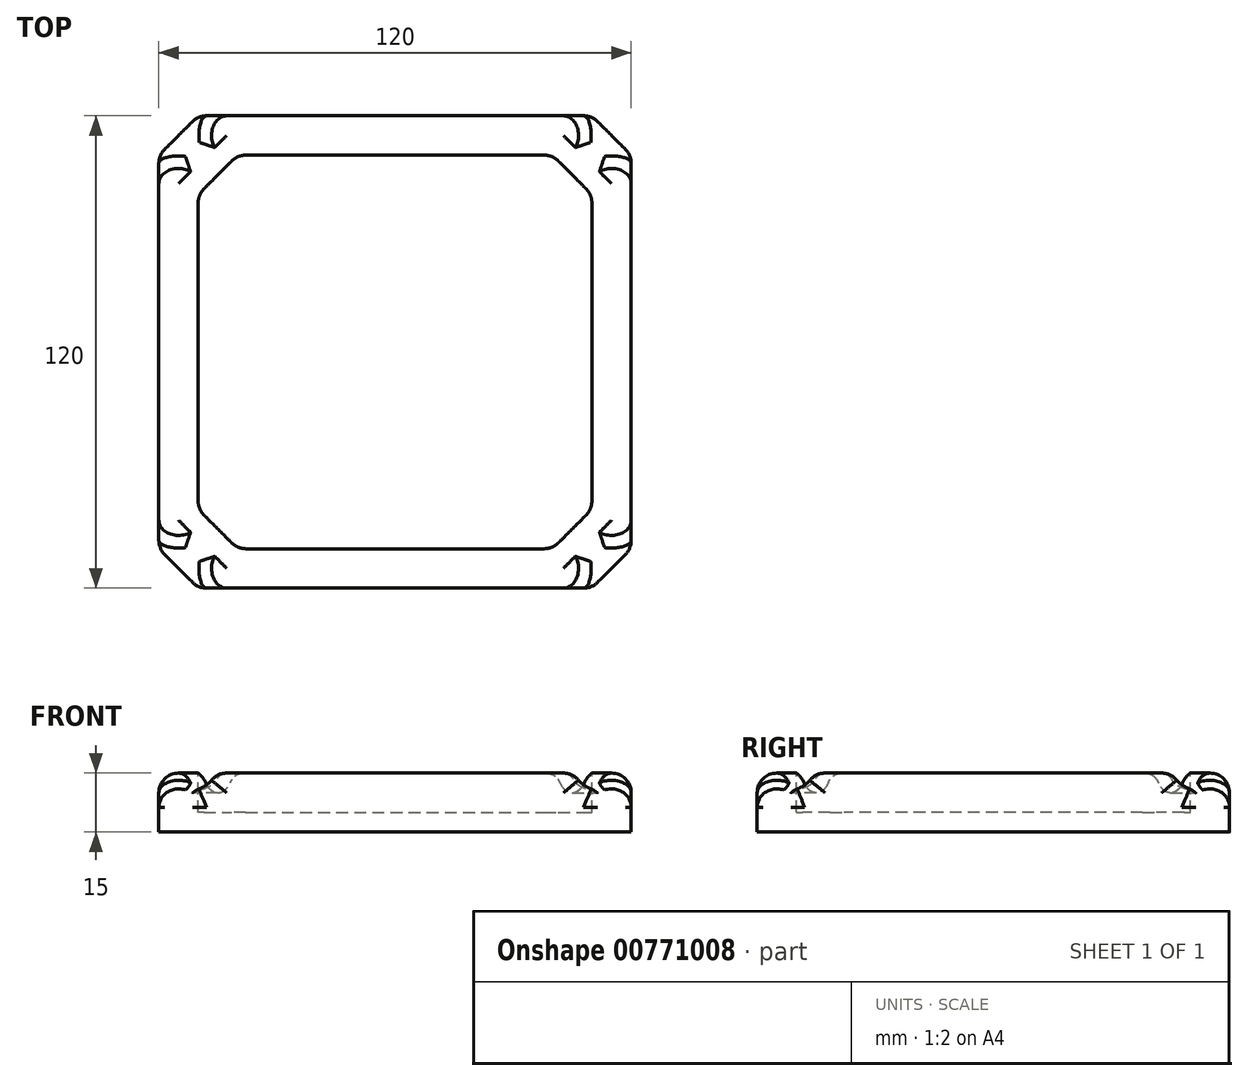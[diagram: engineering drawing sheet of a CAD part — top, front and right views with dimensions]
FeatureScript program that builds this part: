
annotation { "Feature Type Name" : "Feature", "Feature Type Description" : "" }
export const myFeature = defineFeature(function(context is Context, id is Id, definition is map)
    precondition{}
    {
        {
            var Q0;
            Q0=qCreatedBy(makeId("Top.planeOp"),FACE);
            var sketch = newSketch(context, id + "F0", { "sketchPlane" : qUnion([Q0])});
            skLineSegment(sketch, "E0.bottom", {"start": v(-50, 60) * mm, "end": v(50, 60) * mm});
            skLineSegment(sketch, "E0.top", {"start": v(-50, -60) * mm, "end": v(50, -60) * mm});
            skLineSegment(sketch, "E0.left", {"start": v(-60, 50) * mm, "end": v(-60, -50) * mm});
            skLineSegment(sketch, "E0.right", {"start": v(60, 50) * mm, "end": v(60, -50) * mm});
            skLineSegment(sketch, "E1", {"start": v(-60, 50) * mm, "end": v(-50, 60) * mm});
            skLineSegment(sketch, "E2", {"start": v(50, 60) * mm, "end": v(60, 50) * mm});
            skLineSegment(sketch, "E3", {"start": v(60, -50) * mm, "end": v(50, -60) * mm});
            skLineSegment(sketch, "E4", {"start": v(-60, -50) * mm, "end": v(-50, -60) * mm});
            skSolve(sketch);
        }
        {
            var Q0;
            Q0=makeQuery(id+"F0.imprint","IMPRINT",FACE,{"disambiguationData":[TD([[makeQuery(id+"F0.imprint","IMPRINT",EDGE,{"derivedFrom":sQuery(id+"F0.wireOp",EDGE,"E0.bottom")}),-1.0]])]});
            extrude(context, id + "F1", {"entities" : qUnion([Q0]), "depth" : 15 * mm, "offsetDistance" : 25 * mm});
        }
        {
            var Q0;
            Q0=makeQuery(id+"F1.opExtrude","CAP_FACE",FACE,{"disambiguationData":[OSD([sQuery(id+"F0.wireOp",EDGE,"E0.bottom"),sQuery(id+"F0.wireOp",EDGE,"E0.top"),sQuery(id+"F0.wireOp",EDGE,"E0.left"),sQuery(id+"F0.wireOp",EDGE,"E0.right"),sQuery(id+"F0.wireOp",EDGE,"E1"),sQuery(id+"F0.wireOp",EDGE,"E2"),sQuery(id+"F0.wireOp",EDGE,"E3"),sQuery(id+"F0.wireOp",EDGE,"E4")])],"isStart":false});
            var sketch = newSketch(context, id + "F2", { "sketchPlane" : qUnion([Q0])});
            skLineSegment(sketch, "E5.bottom", {"start": v(-40, 50) * mm, "end": v(40, 50) * mm});
            skLineSegment(sketch, "E5.top", {"start": v(-40, -50) * mm, "end": v(40, -50) * mm});
            skLineSegment(sketch, "E5.left", {"start": v(-50, 40) * mm, "end": v(-50, -40) * mm});
            skLineSegment(sketch, "E5.right", {"start": v(50, 40) * mm, "end": v(50, -40) * mm});
            skLineSegment(sketch, "E6", {"start": v(-50, 40) * mm, "end": v(-40, 50) * mm});
            skLineSegment(sketch, "E7", {"start": v(40, 50) * mm, "end": v(50, 40) * mm});
            skLineSegment(sketch, "E8", {"start": v(50, -40) * mm, "end": v(40, -50) * mm});
            skLineSegment(sketch, "E9", {"start": v(-50, -40) * mm, "end": v(-40, -50) * mm});
            skSolve(sketch);
        }
        {
            var Q0;
            Q0=makeQuery(id+"F2.imprint","IMPRINT",FACE,{"disambiguationData":[TD([[makeQuery(id+"F2.imprint","IMPRINT",EDGE,{"derivedFrom":sQuery(id+"F2.wireOp",EDGE,"E5.bottom")}),-1.0]])]});
            extrude(context, id + "F3", {"entities" : qUnion([Q0]), "operationType" : NewBodyOperationType.REMOVE, "oppositeDirection" : true, "depth" : 10 * mm, "offsetDistance" : 25 * mm});
        }
        {
            var Q0;
            Q0=makeQuery(id+"F1.opExtrude","SWEPT_FACE",FACE,{"disambiguationData":[OSD([sQuery(id+"F0.wireOp",EDGE,"E1")])]});
            cPlane(context, id + "F4", {"entities" : qUnion([Q0]), "cplaneType" : CPlaneType.OFFSET, "offset" : .1 * mm, "width" : 150 * mm, "height" : 150 * mm});
        }
        {
            var Q0;
            Q0=qCreatedBy(id+"F4.planeOp",FACE);
            var sketch = newSketch(context, id + "F5", { "sketchPlane" : qUnion([Q0])});
            skCircle(sketch, "E10", {"center": v(0, 15) * mm, "radius": 5 * mm});
            skSolve(sketch);
        }
        {
            var Q0;
            Q0=makeQuery(id+"F5.imprint","IMPRINT",FACE,{"disambiguationData":[TD([[makeQuery(id+"F5.imprint","IMPRINT",EDGE,{"derivedFrom":sQuery(id+"F5.wireOp",EDGE,"E10")}),1.0]])]});
            extrude(context, id + "F6", {"entities" : qUnion([Q0]), "operationType" : NewBodyOperationType.REMOVE, "oppositeDirection" : true, "depth" : 15 * mm, "offsetDistance" : 25 * mm});
        }
        {
            var Q0;
            Q0=makeQuery(id+"F1.opExtrude","SWEPT_FACE",FACE,{"disambiguationData":[OSD([sQuery(id+"F0.wireOp",EDGE,"E2")])]});
            cPlane(context, id + "F7", {"entities" : qUnion([Q0]), "cplaneType" : CPlaneType.OFFSET, "offset" : .1 * mm, "width" : 150 * mm, "height" : 150 * mm});
        }
        {
            var Q0;
            Q0=qCreatedBy(id+"F7.planeOp",FACE);
            var sketch = newSketch(context, id + "F8", { "sketchPlane" : qUnion([Q0])});
            skCircle(sketch, "E11", {"center": v(0, 15) * mm, "radius": 5 * mm});
            skSolve(sketch);
        }
        {
            var Q0;
            Q0=makeQuery(id+"F8.imprint","IMPRINT",FACE,{"disambiguationData":[TD([[makeQuery(id+"F8.imprint","IMPRINT",EDGE,{"derivedFrom":sQuery(id+"F8.wireOp",EDGE,"E11")}),1.0]])]});
            extrude(context, id + "F9", {"entities" : qUnion([Q0]), "operationType" : NewBodyOperationType.REMOVE, "oppositeDirection" : true, "depth" : 15 * mm, "offsetDistance" : 25 * mm});
        }
        {
            var Q0;
            Q0=makeQuery(id+"F1.opExtrude","SWEPT_FACE",FACE,{"disambiguationData":[OSD([sQuery(id+"F0.wireOp",EDGE,"E3")])]});
            cPlane(context, id + "F10", {"entities" : qUnion([Q0]), "cplaneType" : CPlaneType.OFFSET, "offset" : .1 * mm, "width" : 150 * mm, "height" : 150 * mm});
        }
        {
            var Q0;
            Q0=qCreatedBy(id+"F10.planeOp",FACE);
            var sketch = newSketch(context, id + "F11", { "sketchPlane" : qUnion([Q0])});
            skCircle(sketch, "E12", {"center": v(0, 15) * mm, "radius": 5 * mm});
            skSolve(sketch);
        }
        {
            var Q0;
            Q0=makeQuery(id+"F11.imprint","IMPRINT",FACE,{"disambiguationData":[TD([[makeQuery(id+"F11.imprint","IMPRINT",EDGE,{"derivedFrom":sQuery(id+"F11.wireOp",EDGE,"E12")}),1.0]])]});
            extrude(context, id + "F12", {"entities" : qUnion([Q0]), "operationType" : NewBodyOperationType.REMOVE, "oppositeDirection" : true, "depth" : 15 * mm, "offsetDistance" : 25 * mm});
        }
        {
            var Q0;
            Q0=makeQuery(id+"F1.opExtrude","SWEPT_FACE",FACE,{"disambiguationData":[OSD([sQuery(id+"F0.wireOp",EDGE,"E4")])]});
            cPlane(context, id + "F13", {"entities" : qUnion([Q0]), "cplaneType" : CPlaneType.OFFSET, "offset" : .1 * mm, "width" : 150 * mm, "height" : 150 * mm});
        }
        {
            var Q0;
            Q0=qCreatedBy(id+"F13.planeOp",FACE);
            var sketch = newSketch(context, id + "F14", { "sketchPlane" : qUnion([Q0])});
            skCircle(sketch, "E13", {"center": v(0, 15) * mm, "radius": 5 * mm});
            skSolve(sketch);
        }
        {
            var Q0;
            Q0=makeQuery(id+"F14.imprint","IMPRINT",FACE,{"disambiguationData":[TD([[makeQuery(id+"F14.imprint","IMPRINT",EDGE,{"derivedFrom":sQuery(id+"F14.wireOp",EDGE,"E13")}),1.0]])]});
            extrude(context, id + "F15", {"entities" : qUnion([Q0]), "operationType" : NewBodyOperationType.REMOVE, "oppositeDirection" : true, "depth" : 15 * mm, "offsetDistance" : 25 * mm});
        }
        {
            var Q0;
            Q0=makeQuery(id+"F6.boolean.opBoolean","INTERSECT",EDGE,{"disambiguationData":[OD(1.0)],"derivedFrom":[makeQuery(id+"F1.opExtrude","CAP_FACE",FACE,{"disambiguationData":[OSD([sQuery(id+"F0.wireOp",EDGE,"E0.bottom"),sQuery(id+"F0.wireOp",EDGE,"E0.top"),sQuery(id+"F0.wireOp",EDGE,"E0.left"),sQuery(id+"F0.wireOp",EDGE,"E0.right"),sQuery(id+"F0.wireOp",EDGE,"E1"),sQuery(id+"F0.wireOp",EDGE,"E2"),sQuery(id+"F0.wireOp",EDGE,"E3"),sQuery(id+"F0.wireOp",EDGE,"E4")])],"isStart":false}),makeQuery(id+"F6.opExtrude","SWEPT_FACE",FACE,{"disambiguationData":[OSD([sQuery(id+"F5.wireOp",EDGE,"E10")])]})]});
            var Q1;
            Q1=makeQuery(id+"F6.boolean.opBoolean","INTERSECT",EDGE,{"disambiguationData":[OD(0.0)],"derivedFrom":[makeQuery(id+"F1.opExtrude","CAP_FACE",FACE,{"disambiguationData":[OSD([sQuery(id+"F0.wireOp",EDGE,"E0.bottom"),sQuery(id+"F0.wireOp",EDGE,"E0.top"),sQuery(id+"F0.wireOp",EDGE,"E0.left"),sQuery(id+"F0.wireOp",EDGE,"E0.right"),sQuery(id+"F0.wireOp",EDGE,"E1"),sQuery(id+"F0.wireOp",EDGE,"E2"),sQuery(id+"F0.wireOp",EDGE,"E3"),sQuery(id+"F0.wireOp",EDGE,"E4")])],"isStart":false}),makeQuery(id+"F6.opExtrude","SWEPT_FACE",FACE,{"disambiguationData":[OSD([sQuery(id+"F5.wireOp",EDGE,"E10")])]})]});
            var Q2;
            {var subQ5=sQuery(id+"F0.wireOp",EDGE,"E4");var subQ7=sQuery(id+"F0.wireOp",EDGE,"E0.top");var subQ8=makeQuery(id+"F1.opExtrude","SWEPT_FACE",FACE,{"disambiguationData":[OSD([subQ7])]});var subQ10=sQuery(id+"F0.wireOp",EDGE,"E3");var subQ12=sQuery(id+"F0.wireOp",EDGE,"E0.left");var subQ14=sQuery(id+"F0.wireOp",EDGE,"E1");var subQ16=sQuery(id+"F0.wireOp",EDGE,"E2");var subQ17=sQuery(id+"F0.wireOp",EDGE,"E0.right");Q2=makeQuery(id+"F15.boolean.opBoolean","INTERSECT",EDGE,{"disambiguationData":[OD(1.0)],"derivedFrom":[makeQuery(id+"F12.boolean.opBoolean","SPLIT",FACE,{"disambiguationData":[TD([subQ8])],"derivedFrom":makeQuery(id+"F9.boolean.opBoolean","SPLIT",FACE,{"disambiguationData":[TD([subQ8])],"derivedFrom":makeQuery(id+"F1.opExtrude","CAP_FACE",FACE,{"disambiguationData":[OSD([sQuery(id+"F0.wireOp",EDGE,"E0.bottom"),subQ7,subQ12,subQ17,subQ14,subQ16,subQ10,subQ5])],"isStart":false})})}),makeQuery(id+"F15.opExtrude","SWEPT_FACE",FACE,{"disambiguationData":[OSD([sQuery(id+"F14.wireOp",EDGE,"E13")])]})]});}
            var Q3;
            {var subQ5=sQuery(id+"F0.wireOp",EDGE,"E4");var subQ7=sQuery(id+"F0.wireOp",EDGE,"E0.top");var subQ8=makeQuery(id+"F1.opExtrude","SWEPT_FACE",FACE,{"disambiguationData":[OSD([subQ7])]});var subQ10=sQuery(id+"F0.wireOp",EDGE,"E3");var subQ12=sQuery(id+"F0.wireOp",EDGE,"E0.left");var subQ14=sQuery(id+"F0.wireOp",EDGE,"E1");var subQ16=sQuery(id+"F0.wireOp",EDGE,"E2");var subQ17=sQuery(id+"F0.wireOp",EDGE,"E0.right");Q3=makeQuery(id+"F15.boolean.opBoolean","INTERSECT",EDGE,{"disambiguationData":[OD(0.0)],"derivedFrom":[makeQuery(id+"F12.boolean.opBoolean","SPLIT",FACE,{"disambiguationData":[TD([subQ8])],"derivedFrom":makeQuery(id+"F9.boolean.opBoolean","SPLIT",FACE,{"disambiguationData":[TD([subQ8])],"derivedFrom":makeQuery(id+"F1.opExtrude","CAP_FACE",FACE,{"disambiguationData":[OSD([sQuery(id+"F0.wireOp",EDGE,"E0.bottom"),subQ7,subQ12,subQ17,subQ14,subQ16,subQ10,subQ5])],"isStart":false})})}),makeQuery(id+"F15.opExtrude","SWEPT_FACE",FACE,{"disambiguationData":[OSD([sQuery(id+"F14.wireOp",EDGE,"E13")])]})]});}
            var Q4;
            {var subQ0=sQuery(id+"F0.wireOp",EDGE,"E4");var subQ1=sQuery(id+"F0.wireOp",EDGE,"E3");var subQ2=sQuery(id+"F0.wireOp",EDGE,"E2");var subQ3=sQuery(id+"F0.wireOp",EDGE,"E0.top");var subQ4=sQuery(id+"F0.wireOp",EDGE,"E0.left");var subQ5=sQuery(id+"F0.wireOp",EDGE,"E0.right");var subQ6=sQuery(id+"F0.wireOp",EDGE,"E1");Q4=makeQuery(id+"F12.boolean.opBoolean","INTERSECT",EDGE,{"disambiguationData":[OD(0.0)],"derivedFrom":[makeQuery(id+"F9.boolean.opBoolean","SPLIT",FACE,{"disambiguationData":[TD([makeQuery(id+"F1.opExtrude","SWEPT_FACE",FACE,{"disambiguationData":[OSD([subQ3])]})])],"derivedFrom":makeQuery(id+"F1.opExtrude","CAP_FACE",FACE,{"disambiguationData":[OSD([sQuery(id+"F0.wireOp",EDGE,"E0.bottom"),subQ3,subQ4,subQ5,subQ6,subQ2,subQ1,subQ0])],"isStart":false})}),makeQuery(id+"F12.opExtrude","SWEPT_FACE",FACE,{"disambiguationData":[OSD([sQuery(id+"F11.wireOp",EDGE,"E12")])]})]});}
            var Q5;
            {var subQ0=sQuery(id+"F0.wireOp",EDGE,"E4");var subQ1=sQuery(id+"F0.wireOp",EDGE,"E3");var subQ2=sQuery(id+"F0.wireOp",EDGE,"E2");var subQ3=sQuery(id+"F0.wireOp",EDGE,"E0.top");var subQ4=sQuery(id+"F0.wireOp",EDGE,"E0.left");var subQ5=sQuery(id+"F0.wireOp",EDGE,"E0.right");var subQ6=sQuery(id+"F0.wireOp",EDGE,"E1");Q5=makeQuery(id+"F12.boolean.opBoolean","INTERSECT",EDGE,{"disambiguationData":[OD(1.0)],"derivedFrom":[makeQuery(id+"F9.boolean.opBoolean","SPLIT",FACE,{"disambiguationData":[TD([makeQuery(id+"F1.opExtrude","SWEPT_FACE",FACE,{"disambiguationData":[OSD([subQ3])]})])],"derivedFrom":makeQuery(id+"F1.opExtrude","CAP_FACE",FACE,{"disambiguationData":[OSD([sQuery(id+"F0.wireOp",EDGE,"E0.bottom"),subQ3,subQ4,subQ5,subQ6,subQ2,subQ1,subQ0])],"isStart":false})}),makeQuery(id+"F12.opExtrude","SWEPT_FACE",FACE,{"disambiguationData":[OSD([sQuery(id+"F11.wireOp",EDGE,"E12")])]})]});}
            var Q6;
            Q6=makeQuery(id+"F9.boolean.opBoolean","INTERSECT",EDGE,{"disambiguationData":[OD(1.0)],"derivedFrom":[makeQuery(id+"F1.opExtrude","CAP_FACE",FACE,{"disambiguationData":[OSD([sQuery(id+"F0.wireOp",EDGE,"E0.bottom"),sQuery(id+"F0.wireOp",EDGE,"E0.top"),sQuery(id+"F0.wireOp",EDGE,"E0.left"),sQuery(id+"F0.wireOp",EDGE,"E0.right"),sQuery(id+"F0.wireOp",EDGE,"E1"),sQuery(id+"F0.wireOp",EDGE,"E2"),sQuery(id+"F0.wireOp",EDGE,"E3"),sQuery(id+"F0.wireOp",EDGE,"E4")])],"isStart":false}),makeQuery(id+"F9.opExtrude","SWEPT_FACE",FACE,{"disambiguationData":[OSD([sQuery(id+"F8.wireOp",EDGE,"E11")])]})]});
            var Q7;
            Q7=makeQuery(id+"F9.boolean.opBoolean","INTERSECT",EDGE,{"disambiguationData":[OD(0.0)],"derivedFrom":[makeQuery(id+"F1.opExtrude","CAP_FACE",FACE,{"disambiguationData":[OSD([sQuery(id+"F0.wireOp",EDGE,"E0.bottom"),sQuery(id+"F0.wireOp",EDGE,"E0.top"),sQuery(id+"F0.wireOp",EDGE,"E0.left"),sQuery(id+"F0.wireOp",EDGE,"E0.right"),sQuery(id+"F0.wireOp",EDGE,"E1"),sQuery(id+"F0.wireOp",EDGE,"E2"),sQuery(id+"F0.wireOp",EDGE,"E3"),sQuery(id+"F0.wireOp",EDGE,"E4")])],"isStart":false}),makeQuery(id+"F9.opExtrude","SWEPT_FACE",FACE,{"disambiguationData":[OSD([sQuery(id+"F8.wireOp",EDGE,"E11")])]})]});
            fillet(context, id + "F16", {"entities" : qUnion([Q0, Q1, Q2, Q3, Q4, Q5, Q6, Q7]), "radius" : 5 * mm, "tangentPropagation" : true, "allowEdgeOverflow" : false});
        }
        {
            var Q0;
            Q0=makeQuery(id+"F1.opExtrude","SWEPT_EDGE",EDGE,{"disambiguationData":[OSD([sQuery(id+"F0.wireOp",EDGE,"E0.left"),sQuery(id+"F0.wireOp",EDGE,"E1")])]});
            var Q1;
            Q1=makeQuery(id+"F1.opExtrude","SWEPT_EDGE",EDGE,{"disambiguationData":[OSD([sQuery(id+"F0.wireOp",EDGE,"E0.bottom"),sQuery(id+"F0.wireOp",EDGE,"E1")])]});
            var Q2;
            Q2=makeQuery(id+"F1.opExtrude","SWEPT_EDGE",EDGE,{"disambiguationData":[OSD([sQuery(id+"F0.wireOp",EDGE,"E0.left"),sQuery(id+"F0.wireOp",EDGE,"E4")])]});
            var Q3;
            Q3=makeQuery(id+"F1.opExtrude","SWEPT_EDGE",EDGE,{"disambiguationData":[OSD([sQuery(id+"F0.wireOp",EDGE,"E0.top"),sQuery(id+"F0.wireOp",EDGE,"E4")])]});
            var Q4;
            Q4=makeQuery(id+"F1.opExtrude","SWEPT_EDGE",EDGE,{"disambiguationData":[OSD([sQuery(id+"F0.wireOp",EDGE,"E0.top"),sQuery(id+"F0.wireOp",EDGE,"E3")])]});
            var Q5;
            Q5=makeQuery(id+"F1.opExtrude","SWEPT_EDGE",EDGE,{"disambiguationData":[OSD([sQuery(id+"F0.wireOp",EDGE,"E0.right"),sQuery(id+"F0.wireOp",EDGE,"E3")])]});
            var Q6;
            Q6=makeQuery(id+"F1.opExtrude","SWEPT_EDGE",EDGE,{"disambiguationData":[OSD([sQuery(id+"F0.wireOp",EDGE,"E0.right"),sQuery(id+"F0.wireOp",EDGE,"E2")])]});
            var Q7;
            Q7=makeQuery(id+"F1.opExtrude","SWEPT_EDGE",EDGE,{"disambiguationData":[OSD([sQuery(id+"F0.wireOp",EDGE,"E0.bottom"),sQuery(id+"F0.wireOp",EDGE,"E2")])]});
            fillet(context, id + "F17", {"entities" : qUnion([Q0, Q1, Q2, Q3, Q4, Q5, Q6, Q7]), "radius" : 5 * mm, "tangentPropagation" : true, "allowEdgeOverflow" : false});
        }
        {
            var Q0;
            Q0=makeQuery(id+"F3.boolean.opBoolean","COPY",EDGE,{"derivedFrom":makeQuery(id+"F3.opExtrude","SWEPT_EDGE",EDGE,{"disambiguationData":[OSD([sQuery(id+"F2.wireOp",EDGE,"E5.top"),sQuery(id+"F2.wireOp",EDGE,"E9")])]})});
            var Q1;
            Q1=makeQuery(id+"F3.boolean.opBoolean","COPY",EDGE,{"derivedFrom":makeQuery(id+"F3.opExtrude","SWEPT_EDGE",EDGE,{"disambiguationData":[OSD([sQuery(id+"F2.wireOp",EDGE,"E5.left"),sQuery(id+"F2.wireOp",EDGE,"E9")])]})});
            var Q2;
            Q2=makeQuery(id+"F3.boolean.opBoolean","COPY",EDGE,{"derivedFrom":makeQuery(id+"F3.opExtrude","SWEPT_EDGE",EDGE,{"disambiguationData":[OSD([sQuery(id+"F2.wireOp",EDGE,"E5.left"),sQuery(id+"F2.wireOp",EDGE,"E6")])]})});
            var Q3;
            Q3=makeQuery(id+"F3.boolean.opBoolean","COPY",EDGE,{"derivedFrom":makeQuery(id+"F3.opExtrude","SWEPT_EDGE",EDGE,{"disambiguationData":[OSD([sQuery(id+"F2.wireOp",EDGE,"E5.bottom"),sQuery(id+"F2.wireOp",EDGE,"E6")])]})});
            var Q4;
            Q4=makeQuery(id+"F3.boolean.opBoolean","COPY",EDGE,{"derivedFrom":makeQuery(id+"F3.opExtrude","SWEPT_EDGE",EDGE,{"disambiguationData":[OSD([sQuery(id+"F2.wireOp",EDGE,"E5.bottom"),sQuery(id+"F2.wireOp",EDGE,"E7")])]})});
            var Q5;
            Q5=makeQuery(id+"F3.boolean.opBoolean","COPY",EDGE,{"derivedFrom":makeQuery(id+"F3.opExtrude","SWEPT_EDGE",EDGE,{"disambiguationData":[OSD([sQuery(id+"F2.wireOp",EDGE,"E5.right"),sQuery(id+"F2.wireOp",EDGE,"E7")])]})});
            var Q6;
            Q6=makeQuery(id+"F3.boolean.opBoolean","COPY",EDGE,{"derivedFrom":makeQuery(id+"F3.opExtrude","SWEPT_EDGE",EDGE,{"disambiguationData":[OSD([sQuery(id+"F2.wireOp",EDGE,"E5.right"),sQuery(id+"F2.wireOp",EDGE,"E8")])]})});
            var Q7;
            Q7=makeQuery(id+"F3.boolean.opBoolean","COPY",EDGE,{"derivedFrom":makeQuery(id+"F3.opExtrude","SWEPT_EDGE",EDGE,{"disambiguationData":[OSD([sQuery(id+"F2.wireOp",EDGE,"E5.top"),sQuery(id+"F2.wireOp",EDGE,"E8")])]})});
            fillet(context, id + "F18", {"entities" : qUnion([Q0, Q1, Q2, Q3, Q4, Q5, Q6, Q7]), "radius" : 5 * mm, "tangentPropagation" : true, "allowEdgeOverflow" : false});
        }
        {
            var Q0;
            Q0=makeQuery(id+"F1.opExtrude","CAP_EDGE",EDGE,{"disambiguationData":[OSD([sQuery(id+"F0.wireOp",EDGE,"E0.bottom")])],"isStart":false});
            var Q1;
            Q1=makeQuery(id+"F3.boolean.opBoolean","COPY",EDGE,{"derivedFrom":makeQuery(id+"F3.opExtrude","CAP_EDGE",EDGE,{"disambiguationData":[OSD([sQuery(id+"F2.wireOp",EDGE,"E5.bottom")])],"isStart":true})});
            fillet(context, id + "F19", {"entities" : qUnion([Q0, Q1]), "radius" : 5 * mm, "tangentPropagation" : true, "allowEdgeOverflow" : false});
        }
    });
